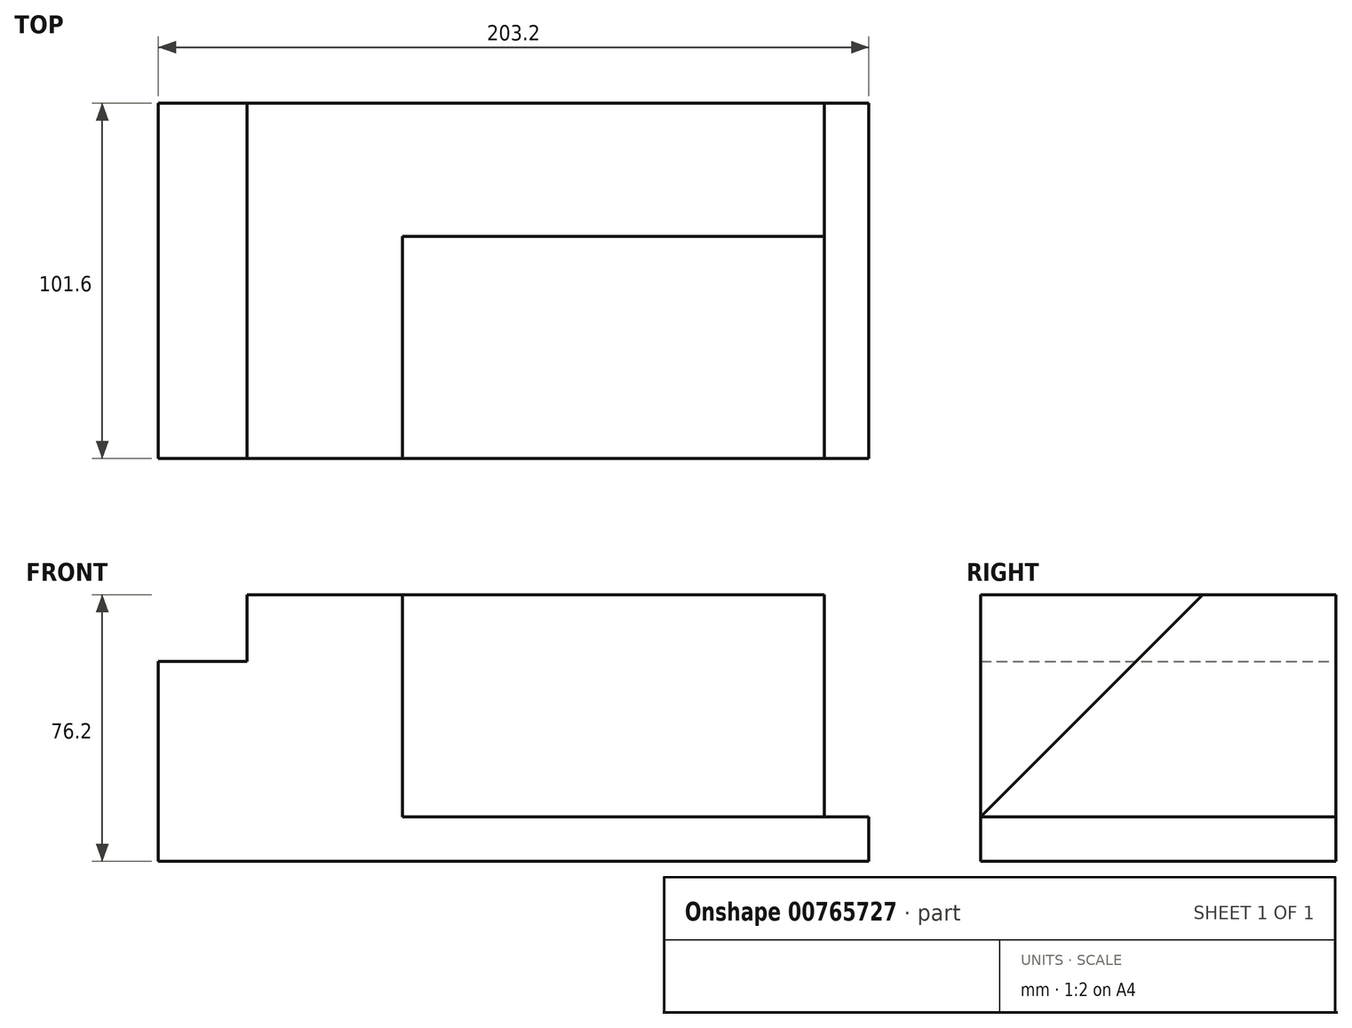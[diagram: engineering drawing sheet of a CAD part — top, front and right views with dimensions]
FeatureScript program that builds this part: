
annotation { "Feature Type Name" : "Feature", "Feature Type Description" : "" }
export const myFeature = defineFeature(function(context is Context, id is Id, definition is map)
    precondition{}
    {
        {
            var Q0;
            Q0=qCreatedBy(makeId("Front.planeOp"),FACE);
            var sketch = newSketch(context, id + "F0", { "sketchPlane" : qUnion([Q0])});
            skLineSegment(sketch, "E0", {"start": v(0, 0) * mm, "end": v(101.6, 0) * mm});
            skLineSegment(sketch, "E1", {"start": v(101.6, 0) * mm, "end": v(101.6, 12.7) * mm});
            skLineSegment(sketch, "E2", {"start": v(101.6, 12.7) * mm, "end": v(88.9, 12.7) * mm});
            skLineSegment(sketch, "E3", {"start": v(88.9, 12.7) * mm, "end": v(88.9, 76.2) * mm});
            skLineSegment(sketch, "E4", {"start": v(88.9, 76.2) * mm, "end": v(-76.2, 76.2) * mm});
            skLineSegment(sketch, "E5", {"start": v(-76.2, 76.2) * mm, "end": v(-76.2, 57.15) * mm});
            skLineSegment(sketch, "E6", {"start": v(-76.2, 57.15) * mm, "end": v(-101.6, 57.15) * mm});
            skLineSegment(sketch, "E7", {"start": v(-101.6, 57.15) * mm, "end": v(-101.6, 0) * mm});
            skLineSegment(sketch, "E8", {"start": v(-101.6, 0) * mm, "end": v(0, 0) * mm});
            skSolve(sketch);
        }
        {
            var Q0;
            Q0=makeQuery(id+"F0.imprint","IMPRINT",FACE,{"disambiguationData":[TD([[makeQuery(id+"F0.imprint","IMPRINT",EDGE,{"derivedFrom":sQuery(id+"F0.wireOp",EDGE,"E0")}),1.0]])]});
            extrude(context, id + "F1", {"entities" : qUnion([Q0]), "depth" : 101.6 * mm, "offsetDistance" : 25.4 * mm});
        }
        {
            var Q0;
            Q0=makeQuery(id+"F1.opExtrude","SWEPT_FACE",FACE,{"disambiguationData":[OSD([sQuery(id+"F0.wireOp",EDGE,"E3")])]});
            var sketch = newSketch(context, id + "F2", { "sketchPlane" : qUnion([Q0])});
            skLineSegment(sketch, "E9", {"start": v(-101.6, 12.7) * mm, "end": v(-38.1, 76.2) * mm});
            skSolve(sketch);
        }
        {
            var Q0;
            {var subQ0=sQuery(id+"F2.wireOp",EDGE,"E9");Q0=makeQuery(id+"F2.imprint","IMPRINT",FACE,{"disambiguationData":[TD([[makeQuery(id+"F2.imprint","IMPRINT",EDGE,{"derivedFrom":subQ0}),1.0]])]});}
            extrude(context, id + "F3", {"entities" : qUnion([Q0]), "operationType" : NewBodyOperationType.REMOVE, "oppositeDirection" : true, "depth" : 120.65 * mm, "offsetDistance" : 25.4 * mm});
        }
    });
